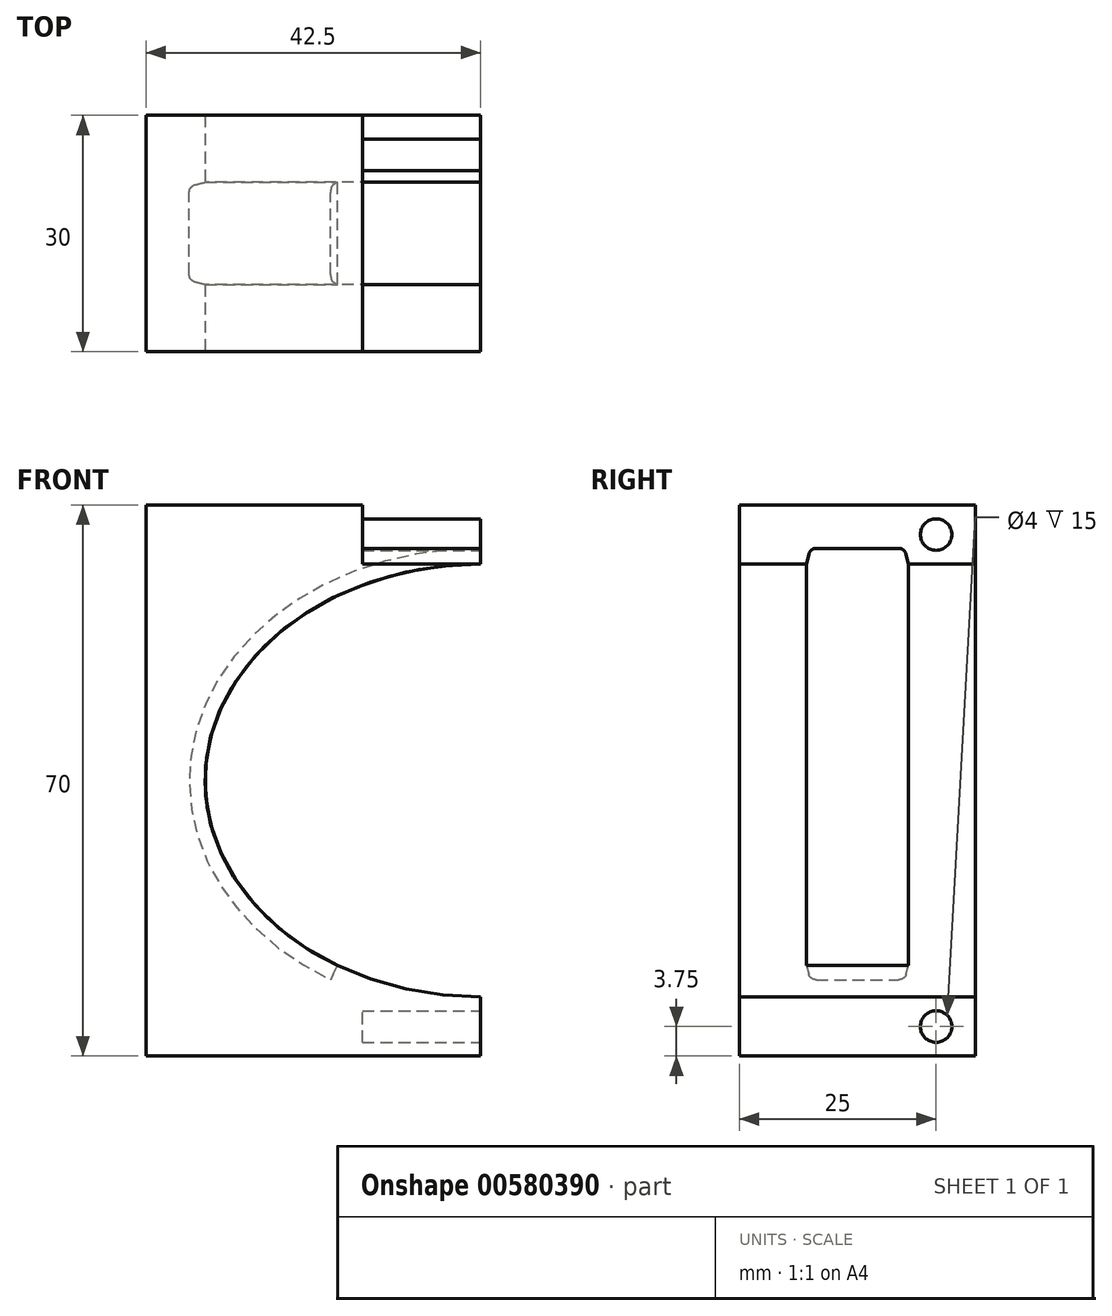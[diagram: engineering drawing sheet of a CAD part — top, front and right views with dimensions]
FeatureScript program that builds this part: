
annotation { "Feature Type Name" : "Feature", "Feature Type Description" : "" }
export const myFeature = defineFeature(function(context is Context, id is Id, definition is map)
    precondition{}
    {
        {
            var Q0;
            Q0=qCreatedBy(makeId("Front.planeOp"),FACE);
            var sketch = newSketch(context, id + "F0", { "sketchPlane" : qUnion([Q0])});
            skEllipse(sketch, "E0", {"center": v(0, 0) * mm, "majorRadius": 35 * mm, "minorRadius": 27.5 * mm, "majorAxis": v(1, 0), "construction": true});
            skSolve(sketch);
        }
        {
            var Q0;
            Q0=qCreatedBy(makeId("Front.planeOp"),FACE);
            var sketch = newSketch(context, id + "F1", { "sketchPlane" : qUnion([Q0])});
            skEllipticalArc(sketch, "E1", {});
            skLineSegment(sketch, "E2", {"start": v(43.16, -27.5) * mm, "end": v(-40.71, -27.5) * mm, "construction": true});
            skLineSegment(sketch, "E3", {"start": v(-18.18, -23.5) * mm, "end": v(18.18, -23.5) * mm, "construction": true});
            skLineSegment(sketch, "E4", {"start": v(0, -23.5) * mm, "end": v(0, 35.22) * mm});
            skPoint(sketch, "E4.endSnap0", {"position": v(0, -23.5) * mm});
            const initialGuessF1  = {"E1": [0, 0, -1, 0, 0.035, 0.0275, 4.71238898038469, 1.0246750333981236]};
            skSetInitialGuess(sketch, initialGuessF1);
            skSolve(sketch);
        }
        {
            var Q0;
            Q0=qCreatedBy(makeId("Front.planeOp"),FACE);
            var sketch = newSketch(context, id + "F2", { "sketchPlane" : qUnion([Q0])});
            skLineSegment(sketch, "E5.bottom", {"start": v(-42.5, 35) * mm, "end": v(42.5, 35) * mm, "construction": true});
            skLineSegment(sketch, "E5.top", {"start": v(-42.5, -35) * mm, "end": v(42.5, -35) * mm, "construction": true});
            skLineSegment(sketch, "E5.left", {"start": v(-42.5, 35) * mm, "end": v(-42.5, -35) * mm});
            skLineSegment(sketch, "E5.right", {"start": v(42.5, 35) * mm, "end": v(42.5, -35) * mm, "construction": true});
            skLineSegment(sketch, "E6", {"start": v(0, 35) * mm, "end": v(0, 27.5) * mm, "construction": true});
            skLineSegment(sketch, "E7", {"start": v(-42.5, 0) * mm, "end": v(0, 0) * mm, "construction": true});
            skLineSegment(sketch, "E8", {"start": v(0, 35) * mm, "end": v(0, 27.5) * mm});
            skLineSegment(sketch, "E9", {"start": v(0, 35) * mm, "end": v(-42.5, 35) * mm});
            skLineSegment(sketch, "E10", {"start": v(-42.5, -35) * mm, "end": v(0, -35) * mm});
            skEllipticalArc(sketch, "E11", {});
            skLineSegment(sketch, "E12.trimOffspring", {"start": v(0, -27.5) * mm, "end": v(0, -35) * mm});
            skLineSegment(sketch, "E13", {"start": v(0, 35) * mm, "end": v(0, 0) * mm, "construction": true});
            const initialGuessF2  = {"E11": [0, 0, 1, 0, 0.035, 0.0275, 1.5707963267948966, 4.71238898038469]};
            skSetInitialGuess(sketch, initialGuessF2);
            skSolve(sketch);
        }
        {
            var Q0;
            Q0=makeQuery(id+"F2.imprint","IMPRINT",FACE,{"disambiguationData":[TD([[makeQuery(id+"F2.imprint","IMPRINT",EDGE,{"derivedFrom":sQuery(id+"F2.wireOp",EDGE,"E5.left")}),1.0]])]});
            extrude(context, id + "F3", {"entities" : qUnion([Q0]), "endBound" : BoundingType.SYMMETRIC, "depth" : 30 * mm, "offsetDistance" : 25 * mm});
        }
        {
            var Q0;
            Q0=makeQuery(id+"F3.opExtrude","SWEPT_FACE",FACE,{"disambiguationData":[OSD([sQuery(id+"F2.wireOp",EDGE,"E8")])]});
            var sketch = newSketch(context, id + "F4", { "sketchPlane" : qUnion([Q0])});
            skLineSegment(sketch, "E14.bottom", {"start": v(-6.5, 27.5) * mm, "end": v(6.5, 27.5) * mm});
            skLineSegment(sketch, "E14.top", {"start": v(-5.22, 29.5) * mm, "end": v(5.22, 29.5) * mm});
            skLineSegment(sketch, "E15", {"start": v(0, 27.5) * mm, "end": v(0, 29.5) * mm, "construction": true});
            skLineSegment(sketch, "E16", {"start": v(-6.5, 27.5) * mm, "end": v(-6.19, 28.74) * mm});
            skLineSegment(sketch, "E17", {"start": v(6.19, 28.74) * mm, "end": v(6.5, 27.5) * mm});
            skPoint(sketch, "E18.visualSharp", {"position": v(-6, 29.5) * mm});
            skArc(sketch, "E18.filletArc", {"start": v(-5.22, 29.5) * mm, "mid": v(-5.83, 29.29) * mm, "end": v(-6.19, 28.74) * mm});
            skPoint(sketch, "E19.visualSharp", {"position": v(6, 29.5) * mm});
            skArc(sketch, "E19.filletArc", {"start": v(6.19, 28.74) * mm, "mid": v(5.83, 29.29) * mm, "end": v(5.22, 29.5) * mm});
            skSolve(sketch);
        }
        {
            var Q0;
            Q0=makeQuery(id+"F4.imprint","IMPRINT",FACE,{"disambiguationData":[TD([[makeQuery(id+"F4.imprint","IMPRINT",EDGE,{"derivedFrom":sQuery(id+"F4.wireOp",EDGE,"E14.bottom")}),1.0]])]});
            var Q1;
            Q1=sQuery(id+"F4.wireOp",EDGE,"E14.top");
            var Q2;
            Q2=sQuery(id+"F1.wireOp",EDGE,"E1");
            sweep(context, id + "F5", {"operationType" : NewBodyOperationType.REMOVE, "profiles" : qUnion([Q0]), "surfaceProfiles" : qUnion([Q1]), "path" : qUnion([Q2])});
        }
        {
            var Q0;
            Q0=makeQuery(id+"F3.opExtrude","SWEPT_FACE",FACE,{"disambiguationData":[OSD([sQuery(id+"F2.wireOp",EDGE,"E8")])]});
            var sketch = newSketch(context, id + "F6", { "sketchPlane" : qUnion([Q0])});
            skLineSegment(sketch, "E20", {"start": v(-15, 31.25) * mm, "end": v(15, 31.25) * mm, "construction": true});
            skLineSegment(sketch, "E21", {"start": v(0, 35) * mm, "end": v(0, 26.42) * mm, "construction": true});
            skPoint(sketch, "E21.endSnap0", {"position": v(0, 29.5) * mm});
            skCircle(sketch, "E22", {"center": v(-10, 31.25) * mm, "radius": 2 * mm});
            skCircle(sketch, "E23.MirrorC", {"center": v(10, 31.25) * mm, "radius": 2 * mm});
            skLineSegment(sketch, "E24", {"start": v(-15, 0) * mm, "end": v(15, 0) * mm, "construction": true});
            skCircle(sketch, "E25.MirrorC", {"center": v(10, -31.25) * mm, "radius": 2 * mm});
            skCircle(sketch, "E26.MirrorC", {"center": v(-10, -31.25) * mm, "radius": 2 * mm});
            skSolve(sketch);
        }
        {
            var Q0;
            Q0=makeQuery(id+"F6.imprint","IMPRINT",FACE,{"disambiguationData":[TD([[makeQuery(id+"F6.imprint","IMPRINT",EDGE,{"derivedFrom":sQuery(id+"F6.wireOp",EDGE,"E23.MirrorC")}),-1.0]])]});
            var Q1;
            Q1=makeQuery(id+"F6.imprint","IMPRINT",FACE,{"disambiguationData":[TD([[makeQuery(id+"F6.imprint","IMPRINT",EDGE,{"derivedFrom":sQuery(id+"F6.wireOp",EDGE,"E22")}),1.0]])]});
            var Q2;
            Q2=makeQuery(id+"F6.imprint","IMPRINT",FACE,{"disambiguationData":[TD([[makeQuery(id+"F6.imprint","IMPRINT",EDGE,{"derivedFrom":sQuery(id+"F6.wireOp",EDGE,"E26.MirrorC")}),-1.0]])]});
            var Q3;
            Q3=makeQuery(id+"F6.imprint","IMPRINT",FACE,{"disambiguationData":[TD([[makeQuery(id+"F6.imprint","IMPRINT",EDGE,{"derivedFrom":sQuery(id+"F6.wireOp",EDGE,"E25.MirrorC")}),1.0]])]});
            extrude(context, id + "F7", {"entities" : qUnion([Q0, Q1, Q2, Q3]), "operationType" : NewBodyOperationType.REMOVE, "oppositeDirection" : true, "depth" : 15 * mm, "offsetDistance" : 25 * mm});
        }
    });
